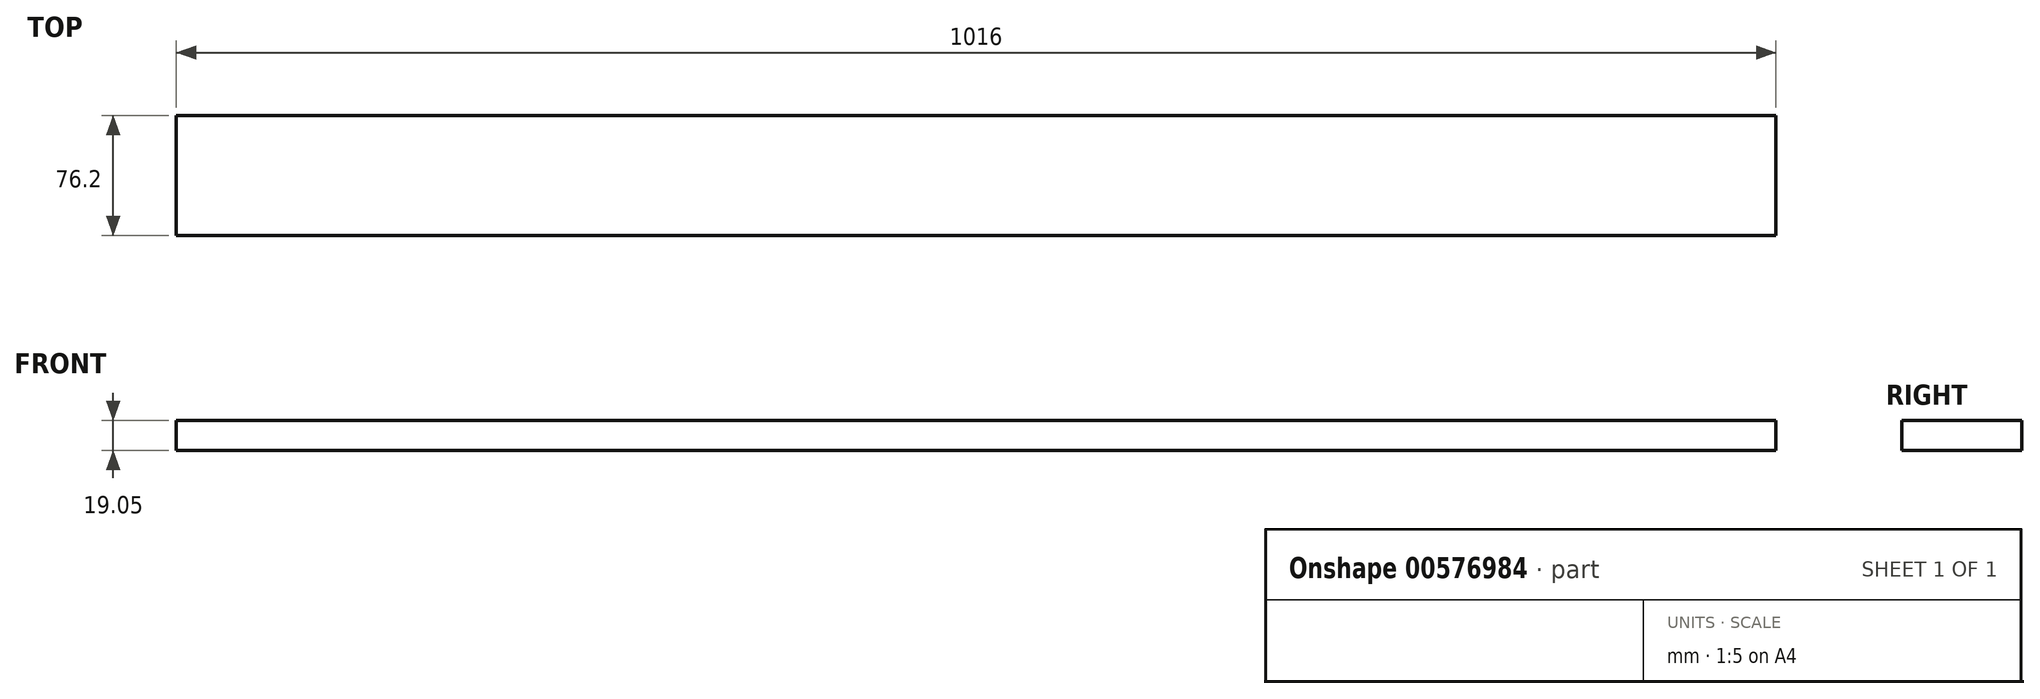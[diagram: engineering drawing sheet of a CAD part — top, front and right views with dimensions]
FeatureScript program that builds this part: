
annotation { "Feature Type Name" : "Feature", "Feature Type Description" : "" }
export const myFeature = defineFeature(function(context is Context, id is Id, definition is map)
    precondition{}
    {
        {
            var Q0;
            Q0=qCreatedBy(makeId("Front.planeOp"),FACE);
            var sketch = newSketch(context, id + "F0", { "sketchPlane" : qUnion([Q0])});
            skLineSegment(sketch, "E0.bottom", {"start": v(0, 0) * mm, "end": v(1016, 0) * mm});
            skLineSegment(sketch, "E0.top", {"start": v(0, 19.05) * mm, "end": v(1016, 19.05) * mm});
            skLineSegment(sketch, "E0.left", {"start": v(0, 0) * mm, "end": v(0, 19.05) * mm});
            skLineSegment(sketch, "E0.right", {"start": v(1016, 0) * mm, "end": v(1016, 19.05) * mm});
            skSolve(sketch);
        }
        {
            var Q0;
            Q0 = qSketchRegion(id + "F0", true);
            extrude(context, id + "F1", {"entities" : qUnion([Q0]), "oppositeDirection" : true, "depth" : 76.2 * mm, "offsetDistance" : 25.4 * mm});
        }
    });
